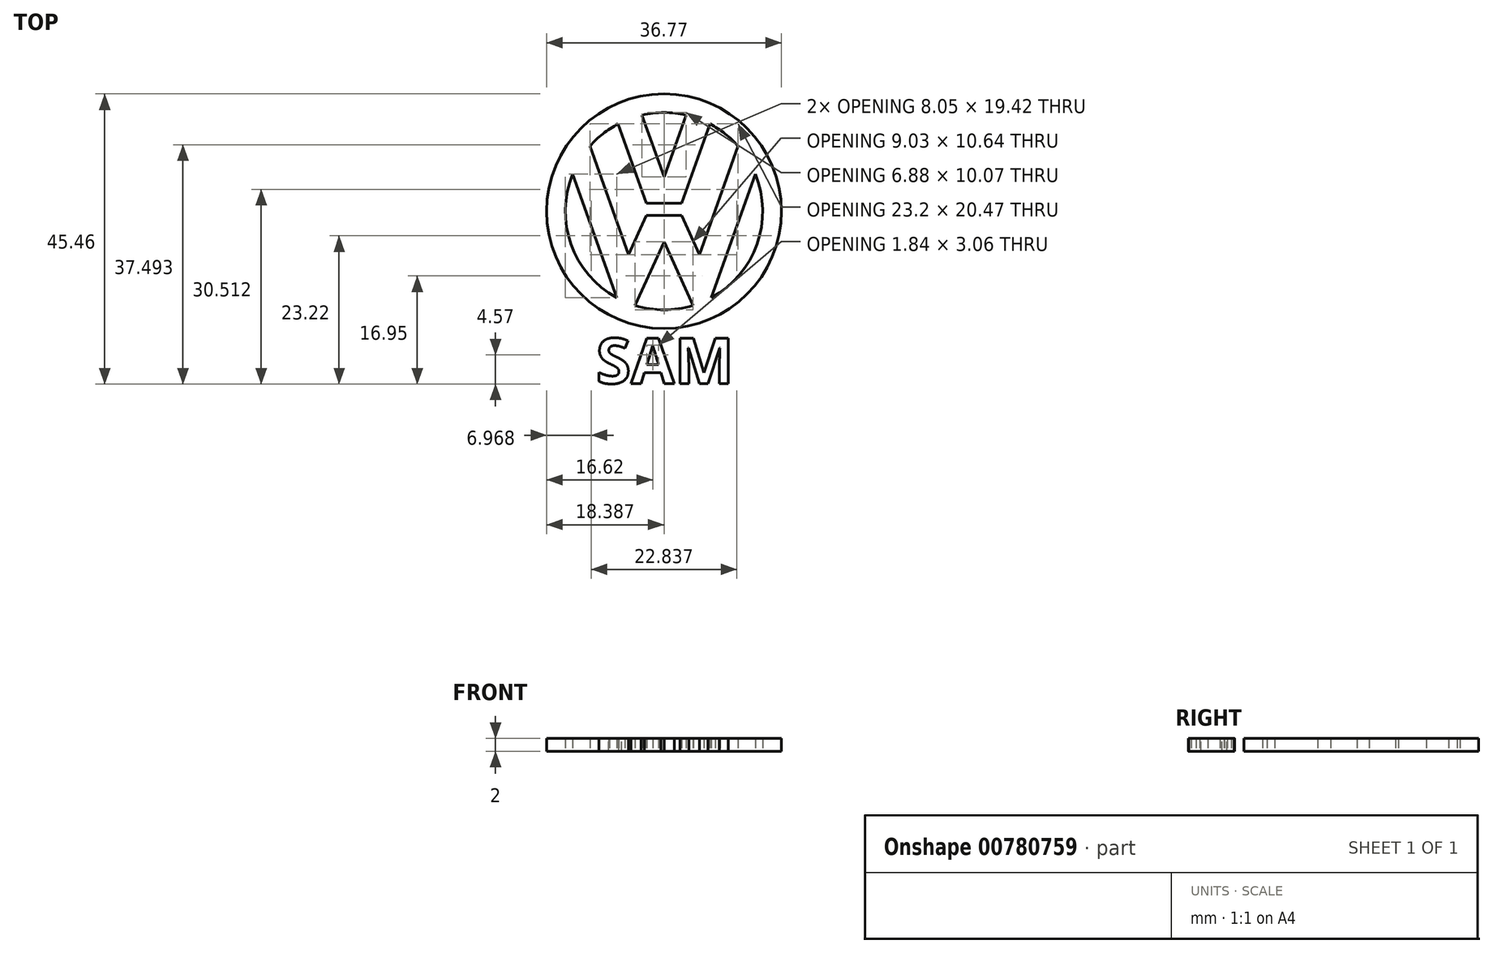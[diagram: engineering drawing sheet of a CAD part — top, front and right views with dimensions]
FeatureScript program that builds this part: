
annotation { "Feature Type Name" : "Feature", "Feature Type Description" : "" }
export const myFeature = defineFeature(function(context is Context, id is Id, definition is map)
    precondition{}
    {
        {
            var Q0;
            Q0=qCreatedBy(makeId("Top.planeOp"),FACE);
            var sketch = newSketch(context, id + "F0", { "sketchPlane" : qUnion([Q0])});
            skPoint(sketch, "E0.centerSnap0", {"position": v(20.78, 41.55) * mm});
            skPoint(sketch, "E0.centerSnap1", {"position": v(41.55, 20.78) * mm});
            skCircle(sketch, "E1", {"center": v(20.78, 20.78) * mm, "radius": 18.38 * mm});
            skArc(sketch, "E2", {"start": v(13.58, 34.45) * mm, "mid": v(11.22, 32.92) * mm, "end": v(9.18, 30.98) * mm});
            skLineSegment(sketch, "E3", {"start": v(18, 22.03) * mm, "end": v(13.58, 34.45) * mm});
            skLineSegment(sketch, "E4", {"start": v(18, 22.03) * mm, "end": v(20.78, 22.03) * mm});
            skLineSegment(sketch, "E5", {"start": v(20.78, 22.03) * mm, "end": v(20.78, 26.16) * mm});
            skLineSegment(sketch, "E6", {"start": v(20.78, 26.16) * mm, "end": v(17.34, 35.84) * mm});
            skLineSegment(sketch, "E7", {"start": v(15.22, 13.98) * mm, "end": v(9.18, 30.98) * mm});
            skLineSegment(sketch, "E8", {"start": v(13.38, 7.21) * mm, "end": v(6.48, 26.63) * mm});
            skLineSegment(sketch, "E9", {"start": v(15.22, 13.98) * mm, "end": v(18, 20.1) * mm});
            skLineSegment(sketch, "E10", {"start": v(18, 20.1) * mm, "end": v(20.78, 20.1) * mm});
            skLineSegment(sketch, "E11", {"start": v(20.78, 20.1) * mm, "end": v(20.78, 15.97) * mm});
            skLineSegment(sketch, "E12", {"start": v(20.78, 15.97) * mm, "end": v(16.26, 6) * mm});
            skArc(sketch, "E13.trimOffspring", {"start": v(6.48, 26.63) * mm, "mid": v(6.22, 15.6) * mm, "end": v(13.38, 7.21) * mm});
            skArc(sketch, "E14.trimOffspring", {"start": v(16.26, 6) * mm, "mid": v(20.78, 5.33) * mm, "end": v(25.3, 6) * mm});
            skLineSegment(sketch, "E15.MirrorCS", {"start": v(20.78, 26.16) * mm, "end": v(24.22, 35.84) * mm});
            skLineSegment(sketch, "E16.MirrorCS", {"start": v(23.55, 22.03) * mm, "end": v(27.97, 34.45) * mm});
            skLineSegment(sketch, "E17.MirrorCS", {"start": v(26.33, 13.98) * mm, "end": v(32.38, 30.98) * mm});
            skLineSegment(sketch, "E18.MirrorCS", {"start": v(28.17, 7.21) * mm, "end": v(35.07, 26.63) * mm});
            skLineSegment(sketch, "E19.MirrorCS", {"start": v(20.78, 15.97) * mm, "end": v(25.3, 6) * mm});
            skLineSegment(sketch, "E20.MirrorCS", {"start": v(26.33, 13.98) * mm, "end": v(23.55, 20.1) * mm});
            skLineSegment(sketch, "E21.MirrorCS", {"start": v(23.55, 22.03) * mm, "end": v(20.78, 22.03) * mm});
            skLineSegment(sketch, "E22.MirrorCS", {"start": v(23.55, 20.1) * mm, "end": v(20.78, 20.1) * mm});
            skArc(sketch, "E23.trimOffspring", {"start": v(24.22, 35.84) * mm, "mid": v(20.78, 36.23) * mm, "end": v(17.34, 35.84) * mm});
            skArc(sketch, "E24.trimOffspring", {"start": v(32.38, 30.98) * mm, "mid": v(30.33, 32.92) * mm, "end": v(27.97, 34.45) * mm});
            skArc(sketch, "E25.trimOffspring", {"start": v(28.17, 7.21) * mm, "mid": v(35.33, 15.6) * mm, "end": v(35.07, 26.63) * mm});
            skText(sketch, "E26", { "text": "SAM", "fontName": "OpenSans-Bold.ttf"});
            skLineSegment(sketch, "E27", {"start": v(20.78, 15.97) * mm, "end": v(20.78, -10.6) * mm, "construction": true});
            const initialGuessF0  = {"E26": [0.01013, -0.0062, 1, 0, 0.00713]};
            skSetInitialGuess(sketch, initialGuessF0);
            skSolve(sketch);
        }
        {
            var Q0;
            Q0=makeQuery(id+"F0.imprint","IMPRINT",FACE,{"disambiguationData":[TD([[makeQuery(id+"F0.imprint","IMPRINT",EDGE,{"derivedFrom":sQuery(id+"F0.wireOp",EDGE,"E26.sketch_text.stroke-0")}),-1.0]])]});
            var Q1;
            Q1=makeQuery(id+"F0.imprint","IMPRINT",FACE,{"disambiguationData":[TD([[makeQuery(id+"F0.imprint","IMPRINT",EDGE,{"derivedFrom":sQuery(id+"F0.wireOp",EDGE,"E26.sketch_text.stroke-28")}),-1.0]])]});
            var Q2;
            Q2=makeQuery(id+"F0.imprint","IMPRINT",FACE,{"disambiguationData":[TD([[makeQuery(id+"F0.imprint","IMPRINT",EDGE,{"derivedFrom":sQuery(id+"F0.wireOp",EDGE,"E26.sketch_text.stroke-40")}),-1.0]])]});
            var Q3;
            Q3=makeQuery(id+"F0.imprint","IMPRINT",FACE,{"disambiguationData":[TD([[makeQuery(id+"F0.imprint","IMPRINT",EDGE,{"derivedFrom":sQuery(id+"F0.wireOp",EDGE,"E1")}),1.0]])]});
            extrude(context, id + "F1", {"entities" : qUnion([Q0, Q1, Q2, Q3]), "depth" : 2 * mm, "offsetDistance" : 25 * mm});
        }
    });
